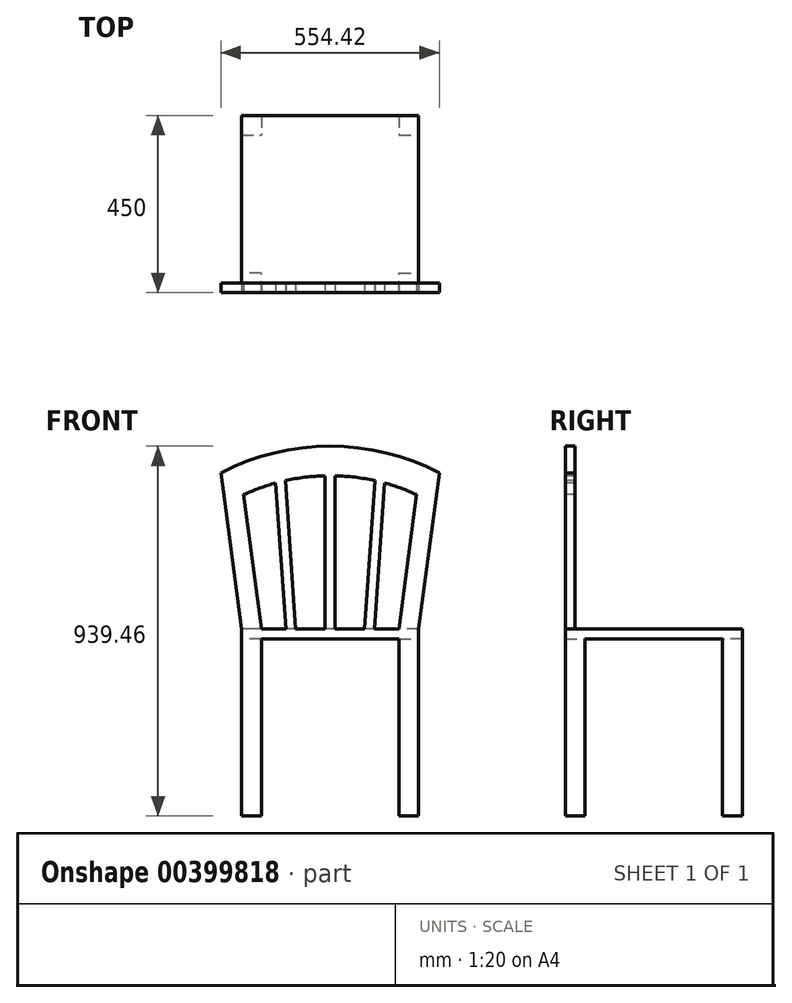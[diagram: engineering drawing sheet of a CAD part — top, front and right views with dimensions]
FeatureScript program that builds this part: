
annotation { "Feature Type Name" : "Feature", "Feature Type Description" : "" }
export const myFeature = defineFeature(function(context is Context, id is Id, definition is map)
    precondition{}
    {
        {
            var Q0;
            Q0=qCreatedBy(makeId("Top.planeOp"),FACE);
            cPlane(context, id + "F0", {"entities" : qUnion([Q0]), "cplaneType" : CPlaneType.OFFSET, "offset" : 450 * mm, "width" : 150 * mm, "height" : 150 * mm});
        }
        {
            var Q0;
            Q0=qCreatedBy(id+"F0.planeOp",FACE);
            var sketch = newSketch(context, id + "F1", { "sketchPlane" : qUnion([Q0])});
            skLineSegment(sketch, "E0.bottom", {"start": v(225, 225) * mm, "end": v(-225, 225) * mm});
            skLineSegment(sketch, "E0.top", {"start": v(225, -225) * mm, "end": v(-225, -225) * mm});
            skLineSegment(sketch, "E0.left", {"start": v(225, 225) * mm, "end": v(225, -225) * mm});
            skLineSegment(sketch, "E0.right", {"start": v(-225, 225) * mm, "end": v(-225, -225) * mm});
            skPoint(sketch, "E0.middle", {"position": v(0, 0) * mm});
            skSolve(sketch);
        }
        {
            var Q0;
            Q0 = qSketchRegion(id + "F1", true);
            extrude(context, id + "F2", {"entities" : qUnion([Q0]), "depth" : 25 * mm});
        }
        {
            var Q0;
            Q0=makeQuery(id+"F2.opExtrude","CAP_FACE",FACE,{"disambiguationData":[OSD([sQuery(id+"F1.wireOp",EDGE,"E0.bottom"),sQuery(id+"F1.wireOp",EDGE,"E0.top"),sQuery(id+"F1.wireOp",EDGE,"E0.left"),sQuery(id+"F1.wireOp",EDGE,"E0.right")])],"isStart":true});
            var sketch = newSketch(context, id + "F3", { "sketchPlane" : qUnion([Q0])});
            skLineSegment(sketch, "E1.bottom", {"start": v(-225, -225) * mm, "end": v(-175, -225) * mm});
            skLineSegment(sketch, "E1.top", {"start": v(-225, -175) * mm, "end": v(-175, -175) * mm});
            skLineSegment(sketch, "E1.left", {"start": v(-225, -225) * mm, "end": v(-225, -175) * mm});
            skLineSegment(sketch, "E1.right", {"start": v(-175, -225) * mm, "end": v(-175, -175) * mm});
            skLineSegment(sketch, "E2.0.1.0", {"start": v(-225, 225) * mm, "end": v(-175, 225) * mm});
            skLineSegment(sketch, "E2.1.0.0", {"start": v(175, -175) * mm, "end": v(225, -175) * mm});
            skLineSegment(sketch, "E2.1.1.0", {"start": v(175, 225) * mm, "end": v(225, 225) * mm});
            skLineSegment(sketch, "E2.direction1", {"start": v(-225, -175) * mm, "end": v(175, -175) * mm, "construction": true});
            skLineSegment(sketch, "E2.direction2", {"start": v(-225, -175) * mm, "end": v(-225, 225) * mm, "construction": true});
            skLineSegment(sketch, "E3", {"start": v(-175, 225) * mm, "end": v(-175, 175) * mm});
            skLineSegment(sketch, "E4", {"start": v(-175, 175) * mm, "end": v(-225, 175) * mm});
            skLineSegment(sketch, "E5", {"start": v(-225, 175) * mm, "end": v(-225, 225) * mm});
            skLineSegment(sketch, "E6", {"start": v(175, 225) * mm, "end": v(175, 175) * mm});
            skLineSegment(sketch, "E7", {"start": v(175, 175) * mm, "end": v(225, 175) * mm});
            skLineSegment(sketch, "E8", {"start": v(225, 175) * mm, "end": v(225, 225) * mm});
            skLineSegment(sketch, "E9", {"start": v(225, -175) * mm, "end": v(225, -225) * mm});
            skLineSegment(sketch, "E10", {"start": v(225, -225) * mm, "end": v(175, -225) * mm});
            skLineSegment(sketch, "E11", {"start": v(175, -225) * mm, "end": v(175, -175) * mm});
            skSolve(sketch);
        }
        {
            var Q0;
            Q0 = qSketchRegion(id + "F3", true);
            var Q1;
            Q1=qCreatedBy(makeId("Top.planeOp"),FACE);
            extrude(context, id + "F4", {"entities" : qUnion([Q0]), "operationType" : NewBodyOperationType.ADD, "endBound" : BoundingType.UP_TO_SURFACE, "endBoundEntityFace" : qUnion([Q1]), "depth" : 25 * mm});
        }
        {
            var Q0;
            Q0=makeQuery(id+"F4.boolean.opBoolean","MERGE",FACE,{"derivedFrom":[makeQuery(id+"F2.opExtrude","SWEPT_FACE",FACE,{"disambiguationData":[OSD([sQuery(id+"F1.wireOp",EDGE,"E0.top")])]}),makeQuery(id+"F4.opExtrude","SWEPT_FACE",FACE,{"disambiguationData":[OSD([sQuery(id+"F3.wireOp",EDGE,"E2.0.1.0")])]}),makeQuery(id+"F4.opExtrude","SWEPT_FACE",FACE,{"disambiguationData":[OSD([sQuery(id+"F3.wireOp",EDGE,"E2.1.1.0")])]})]});
            var sketch = newSketch(context, id + "F5", { "sketchPlane" : qUnion([Q0])});
            skLineSegment(sketch, "E12", {"start": v(-225, 475) * mm, "end": v(-277.21, 871.58) * mm});
            skLineSegment(sketch, "E13", {"start": v(225, 475) * mm, "end": v(277.21, 871.58) * mm});
            skLineSegment(sketch, "E14", {"start": v(-174.57, 475) * mm, "end": v(-219.5, 816.36) * mm});
            skLineSegment(sketch, "E15", {"start": v(174.57, 475) * mm, "end": v(219.5, 816.36) * mm});
            skArc(sketch, "E16", {"start": v(277.21, 871.58) * mm, "mid": v(0, 939.46) * mm, "end": v(-277.21, 871.58) * mm});
            skArc(sketch, "E17", {"start": v(219.5, 816.36) * mm, "mid": v(0, 864.46) * mm, "end": v(-219.5, 816.36) * mm});
            skLineSegment(sketch, "E18", {"start": v(-225, 475) * mm, "end": v(-174.57, 475) * mm});
            skLineSegment(sketch, "E19", {"start": v(174.57, 475) * mm, "end": v(225, 475) * mm});
            skSolve(sketch);
        }
        {
            var Q0;
            Q0 = qSketchRegion(id + "F5", true);
            extrude(context, id + "F6", {"entities" : qUnion([Q0]), "operationType" : NewBodyOperationType.ADD, "oppositeDirection" : true, "depth" : 25 * mm});
        }
        {
            var Q0;
            Q0=makeQuery(id+"F6.boolean.opBoolean","MERGE",FACE,{"derivedFrom":[makeQuery(id+"F4.boolean.opBoolean","MERGE",FACE,{"derivedFrom":[makeQuery(id+"F2.opExtrude","SWEPT_FACE",FACE,{"disambiguationData":[OSD([sQuery(id+"F1.wireOp",EDGE,"E0.top")])]}),makeQuery(id+"F4.opExtrude","SWEPT_FACE",FACE,{"disambiguationData":[OSD([sQuery(id+"F3.wireOp",EDGE,"E2.0.1.0")])]}),makeQuery(id+"F4.opExtrude","SWEPT_FACE",FACE,{"disambiguationData":[OSD([sQuery(id+"F3.wireOp",EDGE,"E2.1.1.0")])]})]}),makeQuery(id+"F6.opExtrude","CAP_FACE",FACE,{"disambiguationData":[OSD([sQuery(id+"F5.wireOp",EDGE,"E12"),sQuery(id+"F5.wireOp",EDGE,"E13"),sQuery(id+"F5.wireOp",EDGE,"E14"),sQuery(id+"F5.wireOp",EDGE,"E15"),sQuery(id+"F5.wireOp",EDGE,"E16"),sQuery(id+"F5.wireOp",EDGE,"E17"),sQuery(id+"F5.wireOp",EDGE,"E18"),sQuery(id+"F5.wireOp",EDGE,"E19")])],"isStart":true})]});
            var sketch = newSketch(context, id + "F7", { "sketchPlane" : qUnion([Q0])});
            skLineSegment(sketch, "E20", {"start": v(0, 864.46) * mm, "end": v(0, 475) * mm, "construction": true});
            skLineSegment(sketch, "E21", {"start": v(-12.5, 864.3) * mm, "end": v(-12.5, 475) * mm});
            skLineSegment(sketch, "E22", {"start": v(-12.5, 475) * mm, "end": v(12.5, 475) * mm});
            skLineSegment(sketch, "E23", {"start": v(12.5, 475) * mm, "end": v(12.5, 864.3) * mm});
            skArc(sketch, "E24", {"start": v(12.5, 864.3) * mm, "mid": v(0, 864.46) * mm, "end": v(-12.5, 864.3) * mm});
            skLineSegment(sketch, "E25", {"start": v(-112.56, 475) * mm, "end": v(-87.5, 475) * mm});
            skLineSegment(sketch, "E26", {"start": v(-87.5, 475) * mm, "end": v(-115.66, 877.67) * mm});
            skLineSegment(sketch, "E27", {"start": v(-112.56, 475) * mm, "end": v(-140.29, 871.53) * mm});
            skArc(sketch, "E28", {"start": v(-140.29, 871.53) * mm, "mid": v(-127.97, 874.57) * mm, "end": v(-115.66, 877.67) * mm});
            skLineSegment(sketch, "E29.MirrorCS", {"start": v(112.56, 475) * mm, "end": v(87.5, 475) * mm});
            skLineSegment(sketch, "E30.MirrorCS", {"start": v(87.5, 475) * mm, "end": v(115.66, 877.67) * mm});
            skArc(sketch, "E31.MirrorCS", {"start": v(140.29, 871.53) * mm, "mid": v(127.97, 874.57) * mm, "end": v(115.66, 877.67) * mm});
            skLineSegment(sketch, "E32.MirrorCS", {"start": v(112.56, 475) * mm, "end": v(140.29, 871.53) * mm});
            skSolve(sketch);
        }
        {
            var Q0;
            Q0 = qSketchRegion(id + "F7", true);
            extrude(context, id + "F8", {"entities" : qUnion([Q0]), "operationType" : NewBodyOperationType.ADD, "oppositeDirection" : true, "depth" : 25 * mm});
        }
    });
